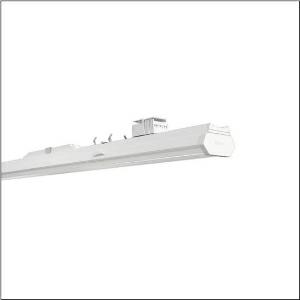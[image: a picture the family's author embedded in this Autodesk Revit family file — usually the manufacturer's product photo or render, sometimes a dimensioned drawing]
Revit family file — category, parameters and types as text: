
# Revit family: licross_r__11_protected_ho_51td12dn4fxm_db4e
name_source: partatom
category: Lighting Fixtures
units: mm (PartAtom-declared; Revit-internal decimal feet)

## family parameters
Cut with Voids When Loaded = No
Host = Face
Light Source = No
Part Type = Normal
Room Calculation Point = No
Round Connector Dimension = Use Diameter
Shared = No

## types (1)
- --- (1 x LED, 15270 lm, 87.3 W, 4000K)
    Apparent Load = 87 VA
    CIE Flux Codes = 70 91 97 98 100
    Color Rendering = 80
    Color Temperature = 4000K
    Default Elevation = 1800 mm
    Description = Licross® 11 Protected HO, luminaire insert, of sheet steel, galvanised, coil coated, white, length: 1.500mm, width: 90mm, height: 101mm, LED rated luminous flux: 15.270lm, light colour: 840, control gear: DALI 2, with plug, 5-pole, with phase selection, mains connection: 220..240V, AC, 50/60Hz, rated input power: 87W, halogen-free wiring, primary optical cover: cover, of PMMA, light emission: direct distribution, primary light characteristic: symmetric, protection rating (complete): IP54, insulation class (complete): insulation class I (protective earthing), certification: CE, ENEC, VDE, UKCA, protection symbol: D if used in an environment with non-conductive dust loads with corresponding accessories, impact resistance: IK06, permissible ambient temperature for indoor applications: -25..+30°C, corresponds to IFS (International Featured Standards) requirements for safety and quality in the food industry, reducing of maximum allowable ambient temperature of 5°C with ceiling mounting, LABS conformity tested according to VDMA 24364:2018-05, packaging unit: 1 piece
    Height = 92 mm
    Lamp = 1 x LED
    Lamp Light Flux = 15270 lm
    Lamp Power = 87.3 W
    Lamp count = 1
    Length = 1500 mm
    Luminous efficacy = 175 lm/W
    Manufacturer = Siteco
    ModVariant = No
    Model = 51TD12DN4FXM
    Mounting Place = Ceiling
    Mounting Type = Pendant
    Number of Poles = 1
    OnlyDefault = Yes
    Power Factor = 1
    Product Name = Licross® 11 Protected HO
    Product group = luminaire insert
    ProductGroupID = 902
    Protection Class = Protection class I
    Protection Degree = IP 54
    RLX_Detail_Level = 1
    RLX_Emergency_Light_Flux = 0 lm
    RLX_Emergency_Type = 0
    RLX_Emergency_Type_DB = No
    RlxData = <blob elided: 24281 chars, md5=af466fd7>
    Socket = socket
    Standby Power = 0 W
    System Light Flux = 15270 lm
    System Power = 87 W
    Type Comments = factory setting: luminous flux: 100 % | dim-lin: 254 | 589 mA
    Type Image = l_1256145.jpg
    URL = http://relux.com
    VarID = @adj_101224
    Voltage = 0 V
    Weight = 0.00 kg
    Width = 88 mm

## geometry (parser evidence)
native form markers: Blend x4, Sweep x11
no freeform markers — native parametric forms only
